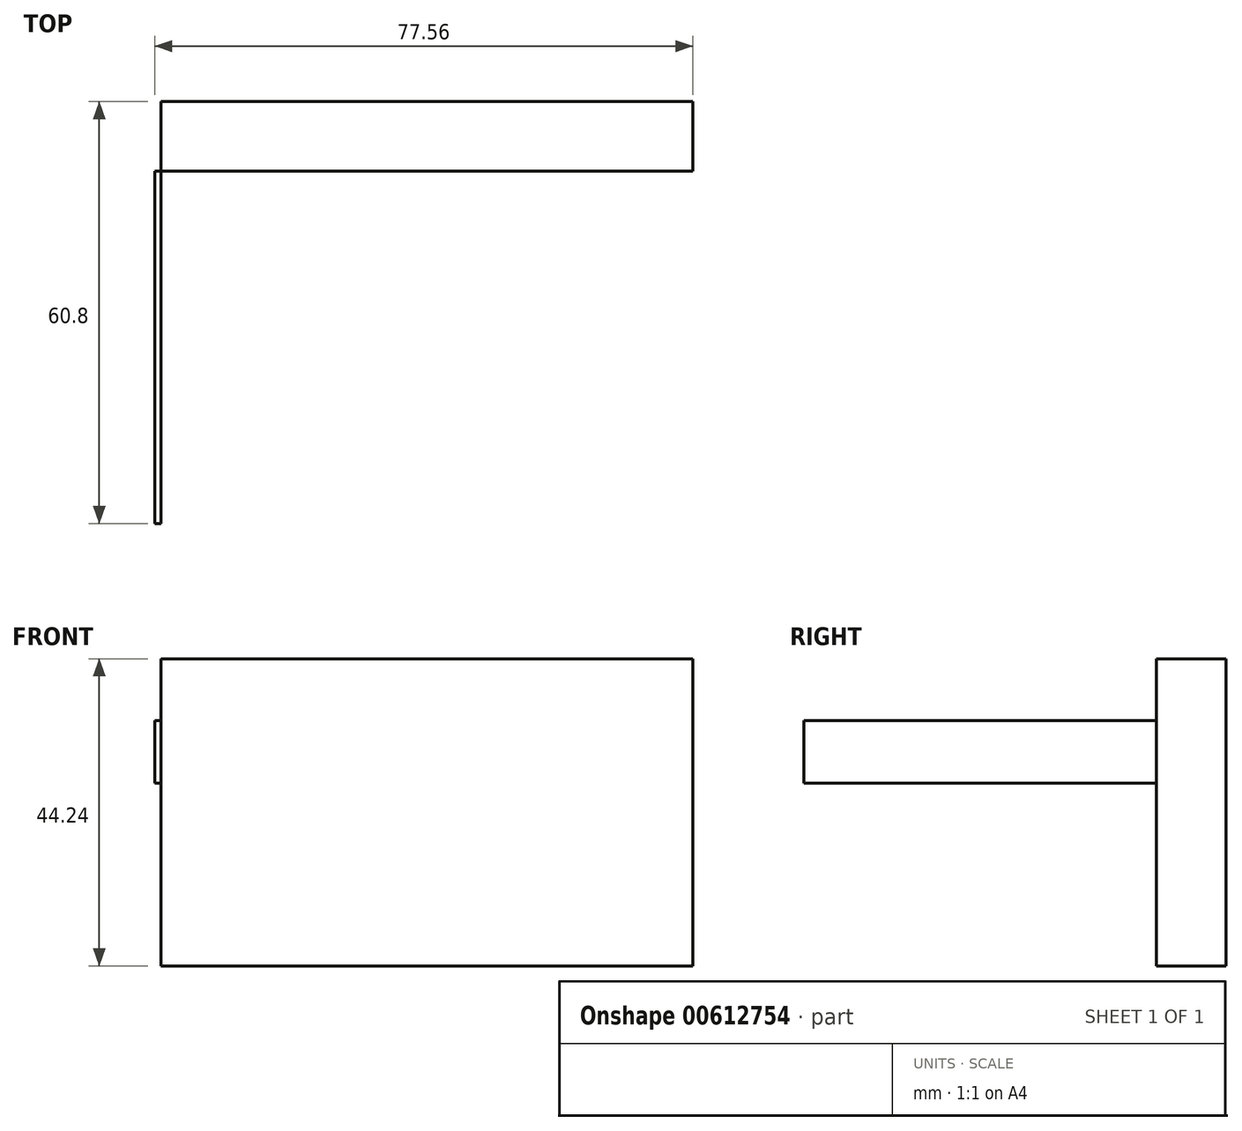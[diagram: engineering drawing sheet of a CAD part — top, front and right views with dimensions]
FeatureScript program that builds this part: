
annotation { "Feature Type Name" : "Feature", "Feature Type Description" : "" }
export const myFeature = defineFeature(function(context is Context, id is Id, definition is map)
    precondition{}
    {
        {
            var Q0;
            Q0=qCreatedBy(makeId("Front.planeOp"),FACE);
            var sketch = newSketch(context, id + "F0", { "sketchPlane" : qUnion([Q0])});
            skLineSegment(sketch, "E0.bottom", {"start": v(38.33, -22.12) * mm, "end": v(-38.33, -22.12) * mm});
            skLineSegment(sketch, "E0.top", {"start": v(38.33, 22.12) * mm, "end": v(-38.33, 22.12) * mm});
            skLineSegment(sketch, "E0.left", {"start": v(38.33, -22.12) * mm, "end": v(38.33, 22.12) * mm});
            skLineSegment(sketch, "E0.right", {"start": v(-38.33, -22.12) * mm, "end": v(-38.33, 22.12) * mm});
            skPoint(sketch, "E0.middle", {"position": v(0, 0) * mm});
            skSolve(sketch);
        }
        {
            var Q0;
            Q0 = qSketchRegion(id + "F0", true);
            extrude(context, id + "F1", {"entities" : qUnion([Q0]), "depth" : 10 * mm, "offsetDistance" : 25.4 * mm});
        }
        {
            var Q0;
            Q0=makeQuery(id+"F1.opExtrude","CAP_FACE",FACE,{"disambiguationData":[OSD([sQuery(id+"F0.wireOp",EDGE,"E0.bottom"),sQuery(id+"F0.wireOp",EDGE,"E0.top"),sQuery(id+"F0.wireOp",EDGE,"E0.left"),sQuery(id+"F0.wireOp",EDGE,"E0.right")])],"isStart":false});
            var sketch = newSketch(context, id + "F2", { "sketchPlane" : qUnion([Q0])});
            skLineSegment(sketch, "E1.bottom", {"start": v(-26.2, 4.2) * mm, "end": v(-39.23, 4.2) * mm});
            skLineSegment(sketch, "E1.top", {"start": v(-26.2, 13.25) * mm, "end": v(-39.23, 13.25) * mm});
            skLineSegment(sketch, "E1.left", {"start": v(-26.2, 4.2) * mm, "end": v(-26.2, 13.25) * mm});
            skLineSegment(sketch, "E1.right", {"start": v(-39.23, 4.2) * mm, "end": v(-39.23, 13.25) * mm});
            skPoint(sketch, "E1.middle", {"position": v(-32.72, 8.73) * mm});
            skSolve(sketch);
        }
        {
            var Q0;
            {var subQ0=sQuery(id+"F2.wireOp",EDGE,"E1.right");Q0=makeQuery(id+"F2.imprint","IMPRINT",FACE,{"disambiguationData":[TD([[makeQuery(id+"F2.imprint","IMPRINT",EDGE,{"derivedFrom":subQ0}),-1.0]])]});}
            extrude(context, id + "F3", {"entities" : qUnion([Q0]), "depth" : 25.4 * mm, "offsetDistance" : 25.4 * mm});
        }
        {
            var Q0;
            Q0=makeQuery(id+"F3.opExtrude","CAP_FACE",FACE,{"disambiguationData":[OSD([sQuery(id+"F0.wireOp",EDGE,"E0.right"),sQuery(id+"F2.wireOp",EDGE,"E1.bottom"),sQuery(id+"F2.wireOp",EDGE,"E1.top"),sQuery(id+"F2.wireOp",EDGE,"E1.right")])],"isStart":false});
            extrude(context, id + "F4", {"entities" : qUnion([Q0]), "operationType" : NewBodyOperationType.ADD, "depth" : 25.4 * mm, "offsetDistance" : 25.4 * mm});
        }
    });
